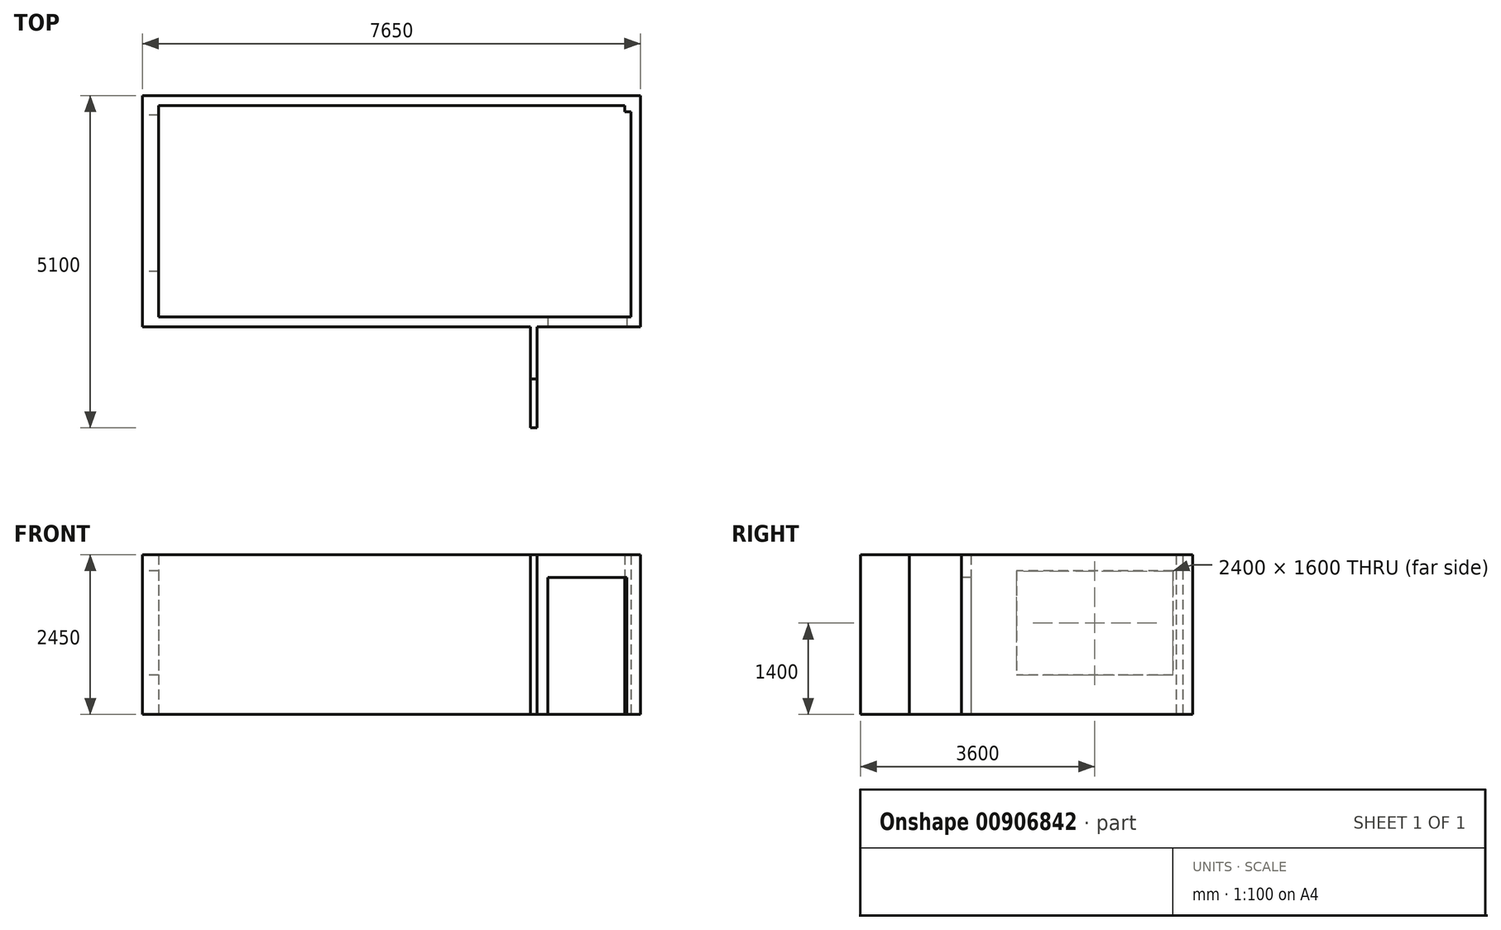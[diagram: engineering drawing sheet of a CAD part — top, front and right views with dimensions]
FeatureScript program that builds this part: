
annotation { "Feature Type Name" : "Feature", "Feature Type Description" : "" }
export const myFeature = defineFeature(function(context is Context, id is Id, definition is map)
    precondition{}
    {
        {
            var Q0;
            Q0=qCreatedBy(makeId("Top.planeOp"),FACE);
            var sketch = newSketch(context, id + "F0", { "sketchPlane" : qUnion([Q0])});
            skLineSegment(sketch, "E0.bottom", {"start": v(-3428.48, -1635.54) * mm, "end": v(3821.52, -1635.54) * mm});
            skLineSegment(sketch, "E0.top", {"start": v(-3428.48, 1614.46) * mm, "end": v(3821.52, 1614.46) * mm});
            skLineSegment(sketch, "E0.left", {"start": v(-3428.48, -1635.54) * mm, "end": v(-3428.48, 1614.46) * mm});
            skLineSegment(sketch, "E0.right", {"start": v(3821.52, -1635.54) * mm, "end": v(3821.52, 1614.46) * mm});
            skLineSegment(sketch, "E1.0", {"start": v(-3578.48, 1764.46) * mm, "end": v(3971.52, 1764.46) * mm});
            skLineSegment(sketch, "E1.1", {"start": v(-3578.48, -1785.54) * mm, "end": v(-3578.48, 1764.46) * mm});
            skLineSegment(sketch, "E1.2", {"start": v(-3578.48, -1785.54) * mm, "end": v(3971.52, -1785.54) * mm});
            skLineSegment(sketch, "E1.3", {"start": v(3971.52, -1785.54) * mm, "end": v(3971.52, 1764.46) * mm});
            skSolve(sketch);
        }
        {
            var Q0;
            Q0=makeQuery(id+"F0.imprint","IMPRINT",FACE,{"disambiguationData":[TD([[makeQuery(id+"F0.imprint","IMPRINT",EDGE,{"derivedFrom":sQuery(id+"F0.wireOp",EDGE,"E0.bottom")}),-1.0]])]});
            extrude(context, id + "F1", {"entities" : qUnion([Q0]), "depth" : 2450 * mm, "offsetDistance" : 25 * mm});
        }
        {
            var Q0;
            Q0=makeQuery(id+"F1.opExtrude","SWEPT_FACE",FACE,{"disambiguationData":[OSD([sQuery(id+"F0.wireOp",EDGE,"E1.2")])]});
            var sketch = newSketch(context, id + "F2", { "sketchPlane" : qUnion([Q0])});
            skLineSegment(sketch, "E2", {"start": v(3759.1, 0) * mm, "end": v(3759.1, 2100.65) * mm});
            skLineSegment(sketch, "E3", {"start": v(3759.1, 2100.65) * mm, "end": v(2547.71, 2100.65) * mm});
            skLineSegment(sketch, "E4", {"start": v(2547.71, 2100.65) * mm, "end": v(2547.71, 0) * mm});
            skSolve(sketch);
        }
        {
            var Q0;
            {var subQ0=sQuery(id+"F2.wireOp",EDGE,"E2");Q0=makeQuery(id+"F2.imprint","IMPRINT",FACE,{"disambiguationData":[TD([[makeQuery(id+"F2.imprint","IMPRINT",EDGE,{"derivedFrom":subQ0}),1.0]])]});}
            extrude(context, id + "F3", {"entities" : qUnion([Q0]), "operationType" : NewBodyOperationType.REMOVE, "oppositeDirection" : true, "depth" : 150 * mm, "offsetDistance" : 25 * mm});
        }
        {
            var Q0;
            Q0=makeQuery(id+"F1.opExtrude","SWEPT_FACE",FACE,{"disambiguationData":[OSD([sQuery(id+"F0.wireOp",EDGE,"E1.1")])]});
            var sketch = newSketch(context, id + "F4", { "sketchPlane" : qUnion([Q0])});
            skLineSegment(sketch, "E5.bottom", {"start": v(-1464.46, 2200) * mm, "end": v(935.54, 2200) * mm});
            skLineSegment(sketch, "E5.top", {"start": v(-1464.46, 600) * mm, "end": v(935.54, 600) * mm});
            skLineSegment(sketch, "E5.left", {"start": v(-1464.46, 2200) * mm, "end": v(-1464.46, 600) * mm});
            skLineSegment(sketch, "E5.right", {"start": v(935.54, 2200) * mm, "end": v(935.54, 600) * mm});
            skSolve(sketch);
        }
        {
            var Q0;
            Q0 = qSketchRegion(id + "F4", true);
            extrude(context, id + "F5", {"entities" : qUnion([Q0]), "operationType" : NewBodyOperationType.REMOVE, "oppositeDirection" : true, "depth" : 150 * mm, "offsetDistance" : 25 * mm});
        }
        {
            var Q0;
            Q0=makeQuery(id+"F1.opExtrude","SWEPT_FACE",FACE,{"disambiguationData":[OSD([sQuery(id+"F0.wireOp",EDGE,"E1.1")])]});
            extrude(context, id + "F6", {"entities" : qUnion([Q0]), "operationType" : NewBodyOperationType.ADD, "depth" : 100 * mm, "offsetDistance" : 25 * mm});
        }
        {
            var Q0;
            Q0=makeQuery(id+"F1.opExtrude","SWEPT_FACE",FACE,{"disambiguationData":[OSD([sQuery(id+"F0.wireOp",EDGE,"E0.top")])]});
            var sketch = newSketch(context, id + "F7", { "sketchPlane" : qUnion([Q0])});
            skLineSegment(sketch, "E6", {"start": v(3728.76, 2450) * mm, "end": v(3728.76, 0) * mm});
            skSolve(sketch);
        }
        {
            var Q0;
            {var subQ0=sQuery(id+"F7.wireOp",EDGE,"E6");Q0=makeQuery(id+"F7.imprint","IMPRINT",FACE,{"disambiguationData":[TD([[makeQuery(id+"F7.imprint","IMPRINT",EDGE,{"derivedFrom":subQ0}),1.0]])]});}
            extrude(context, id + "F8", {"entities" : qUnion([Q0]), "operationType" : NewBodyOperationType.ADD, "depth" : 100 * mm, "offsetDistance" : 25 * mm});
        }
        {
            var Q0;
            {var subQ0=sQuery(id+"F0.wireOp",EDGE,"E1.2");Q0=makeQuery(id+"F6.boolean.opBoolean","MERGE",FACE,{"derivedFrom":[makeQuery(id+"F1.opExtrude","SWEPT_FACE",FACE,{"disambiguationData":[OSD([subQ0])]}),makeQuery(id+"F6.opExtrude","SWEPT_FACE",FACE,{"disambiguationData":[OSD([sQuery(id+"F0.wireOp",EDGE,"E1.1"),subQ0])]})]});}
            var sketch = newSketch(context, id + "F9", { "sketchPlane" : qUnion([Q0])});
            skLineSegment(sketch, "E7", {"start": v(2382.8, 0) * mm, "end": v(2382.8, 2450) * mm});
            skLineSegment(sketch, "E8.0", {"start": v(2282.8, 0) * mm, "end": v(2282.8, 2450) * mm});
            skSolve(sketch);
        }
        {
            var Q0;
            {var subQ0=sQuery(id+"F9.wireOp",EDGE,"E7");Q0=makeQuery(id+"F9.imprint","IMPRINT",FACE,{"disambiguationData":[TD([[makeQuery(id+"F9.imprint","IMPRINT",EDGE,{"derivedFrom":subQ0}),1.0]])]});}
            extrude(context, id + "F10", {"entities" : qUnion([Q0]), "operationType" : NewBodyOperationType.ADD, "depth" : 800 * mm, "offsetDistance" : 25 * mm});
        }
        {
            var Q0;
            Q0=makeQuery(id+"F10.opExtrude","CAP_FACE",FACE,{"disambiguationData":[OSD([sQuery(id+"F0.wireOp",EDGE,"E1.1"),sQuery(id+"F0.wireOp",EDGE,"E1.2"),sQuery(id+"F9.wireOp",EDGE,"E7"),sQuery(id+"F9.wireOp",EDGE,"E8.0")])],"isStart":false});
            extrude(context, id + "F11", {"entities" : qUnion([Q0]), "depth" : 750 * mm, "offsetDistance" : 25 * mm});
        }
    });
